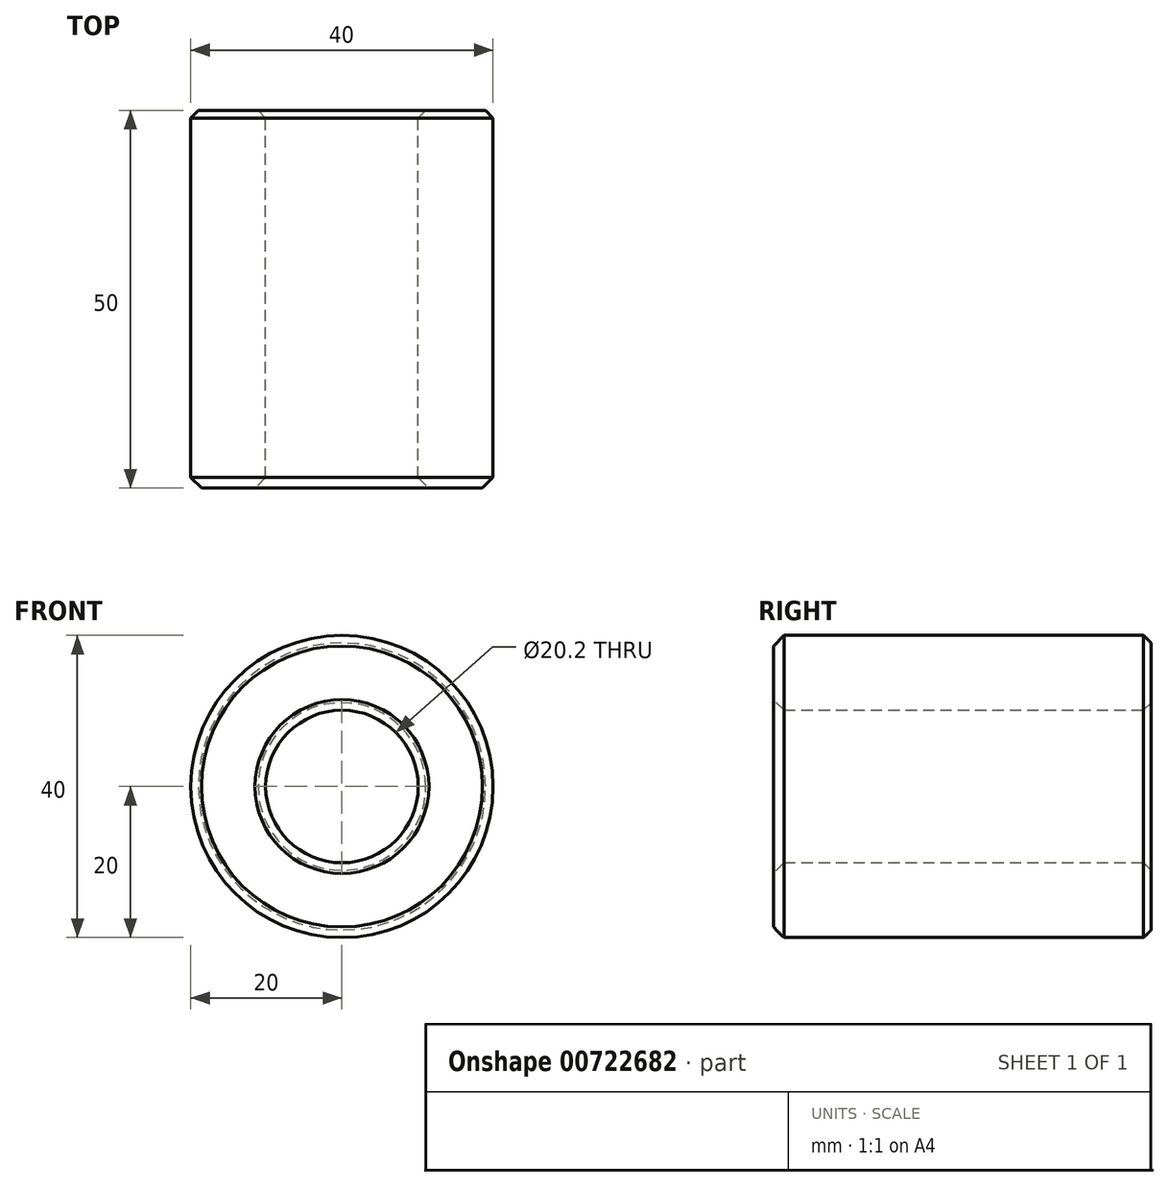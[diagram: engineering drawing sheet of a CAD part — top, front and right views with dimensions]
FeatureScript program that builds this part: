
annotation { "Feature Type Name" : "Feature", "Feature Type Description" : "" }
export const myFeature = defineFeature(function(context is Context, id is Id, definition is map)
    precondition{}
    {
        {
            var Q0;
            Q0=qCreatedBy(makeId("Front.planeOp"),FACE);
            var sketch = newSketch(context, id + "F0", { "sketchPlane" : qUnion([Q0])});
            skCircle(sketch, "E0", {"center": v(0, 0) * mm, "radius": 20 * mm});
            skCircle(sketch, "E1", {"center": v(0, 0) * mm, "radius": 10.1 * mm});
            skSolve(sketch);
        }
        {
            var Q0;
            Q0=makeQuery(id+"F0.imprint","IMPRINT",FACE,{"disambiguationData":[TD([[makeQuery(id+"F0.imprint","IMPRINT",EDGE,{"derivedFrom":sQuery(id+"F0.wireOp",EDGE,"E0")}),1.0]])]});
            extrude(context, id + "F1", {"entities" : qUnion([Q0]), "depth" : 50 * mm, "offsetDistance" : 25 * mm, "symmetric" : true});
        }
        {
            var Q0;
            Q0=makeQuery(id+"F1.opExtrude","CAP_EDGE",EDGE,{"disambiguationData":[OSD([sQuery(id+"F0.wireOp",EDGE,"E0")])],"isStart":false});
            var Q1;
            Q1=makeQuery(id+"F1.opExtrude","CAP_EDGE",EDGE,{"disambiguationData":[OSD([sQuery(id+"F0.wireOp",EDGE,"E1")])],"isStart":false});
            chamfer(context, id + "F2", {"entities" : qUnion([Q0, Q1]), "chamferType" : ChamferType.OFFSET_ANGLE, "width" : 1.4 * mm, "oppositeDirection" : false, "angle" : 45 * degree, "tangentPropagation" : true});
        }
        {
            var Q0;
            Q0=makeQuery(id+"F1.opExtrude","CAP_EDGE",EDGE,{"disambiguationData":[OSD([sQuery(id+"F0.wireOp",EDGE,"E1")])],"isStart":true});
            var Q1;
            Q1=makeQuery(id+"F1.opExtrude","CAP_EDGE",EDGE,{"disambiguationData":[OSD([sQuery(id+"F0.wireOp",EDGE,"E0")])],"isStart":true});
            chamfer(context, id + "F3", {"entities" : qUnion([Q0, Q1]), "chamferType" : ChamferType.OFFSET_ANGLE, "width" : 1 * mm, "oppositeDirection" : false, "angle" : 45 * degree, "tangentPropagation" : true});
        }
    });
